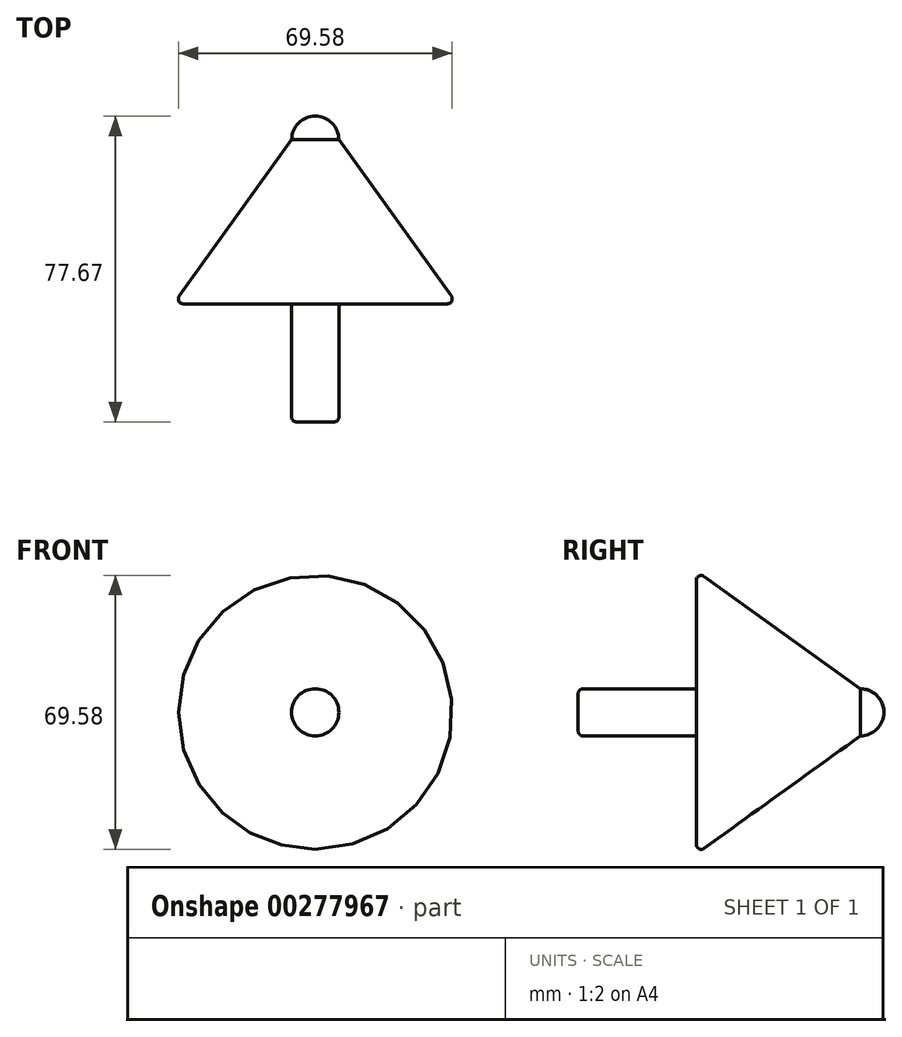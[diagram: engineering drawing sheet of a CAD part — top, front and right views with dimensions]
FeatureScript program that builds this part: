
annotation { "Feature Type Name" : "Feature", "Feature Type Description" : "" }
export const myFeature = defineFeature(function(context is Context, id is Id, definition is map)
    precondition{}
    {
        {
            var Q0;
            Q0=qCreatedBy(makeId("Right.planeOp"),FACE);
            var sketch = newSketch(context, id + "F0", { "sketchPlane" : qUnion([Q0])});
            skLineSegment(sketch, "E0", {"start": v(30, 33.52) * mm, "end": v(30, 6) * mm});
            skLineSegment(sketch, "E1", {"start": v(30, 6) * mm, "end": v(1.27, 6) * mm});
            skLineSegment(sketch, "E2", {"start": v(0, 4.73) * mm, "end": v(0, 1.27) * mm});
            skLineSegment(sketch, "E3", {"start": v(1.27, 0) * mm, "end": v(39.93, 0) * mm, "construction": true});
            skLineSegment(sketch, "E4", {"start": v(0, 0) * mm, "end": v(80, 0) * mm});
            skLineSegment(sketch, "E5", {"start": v(39.93, 0) * mm, "end": v(92.01, 0) * mm, "construction": true});
            skPoint(sketch, "E5.endSnap0", {"position": v(40, 0) * mm});
            skLineSegment(sketch, "E6", {"start": v(71.68, 0) * mm, "end": v(71.68, 5.99) * mm, "construction": true});
            skArc(sketch, "E7", {"start": v(71.68, 5.99) * mm, "mid": v(75.92, 4.24) * mm, "end": v(77.67, 0) * mm});
            skLineSegment(sketch, "E8.trimOffspring", {"start": v(71.68, 5.99) * mm, "end": v(32.01, 34.55) * mm});
            skPoint(sketch, "E9.visualSharp", {"position": v(30, 36) * mm});
            skArc(sketch, "E9.filletArc", {"start": v(32.01, 34.55) * mm, "mid": v(30.7, 34.65) * mm, "end": v(30, 33.52) * mm});
            skPoint(sketch, "E10.visualSharp", {"position": v(0, 6) * mm});
            skArc(sketch, "E10.filletArc", {"start": v(1.27, 6) * mm, "mid": v(0.37, 5.63) * mm, "end": v(0, 4.73) * mm});
            skPoint(sketch, "E11.visualSharp", {"position": v(0, 0) * mm});
            skArc(sketch, "E11.filletArc", {"start": v(0, 1.27) * mm, "mid": v(0.37, 0.37) * mm, "end": v(1.27, 0) * mm});
            skSolve(sketch);
        }
        {
            var Q0;
            Q0 = qSketchRegion(id + "F0", true);
            var Q1;
            Q1=sQuery(id+"F0.wireOp",EDGE,"E5");
            revolve(context, id + "F1", {"entities" : qUnion([Q0]), "axis" : qUnion([Q1]), "revolveType" : RevolveType.FULL});
        }
    });
